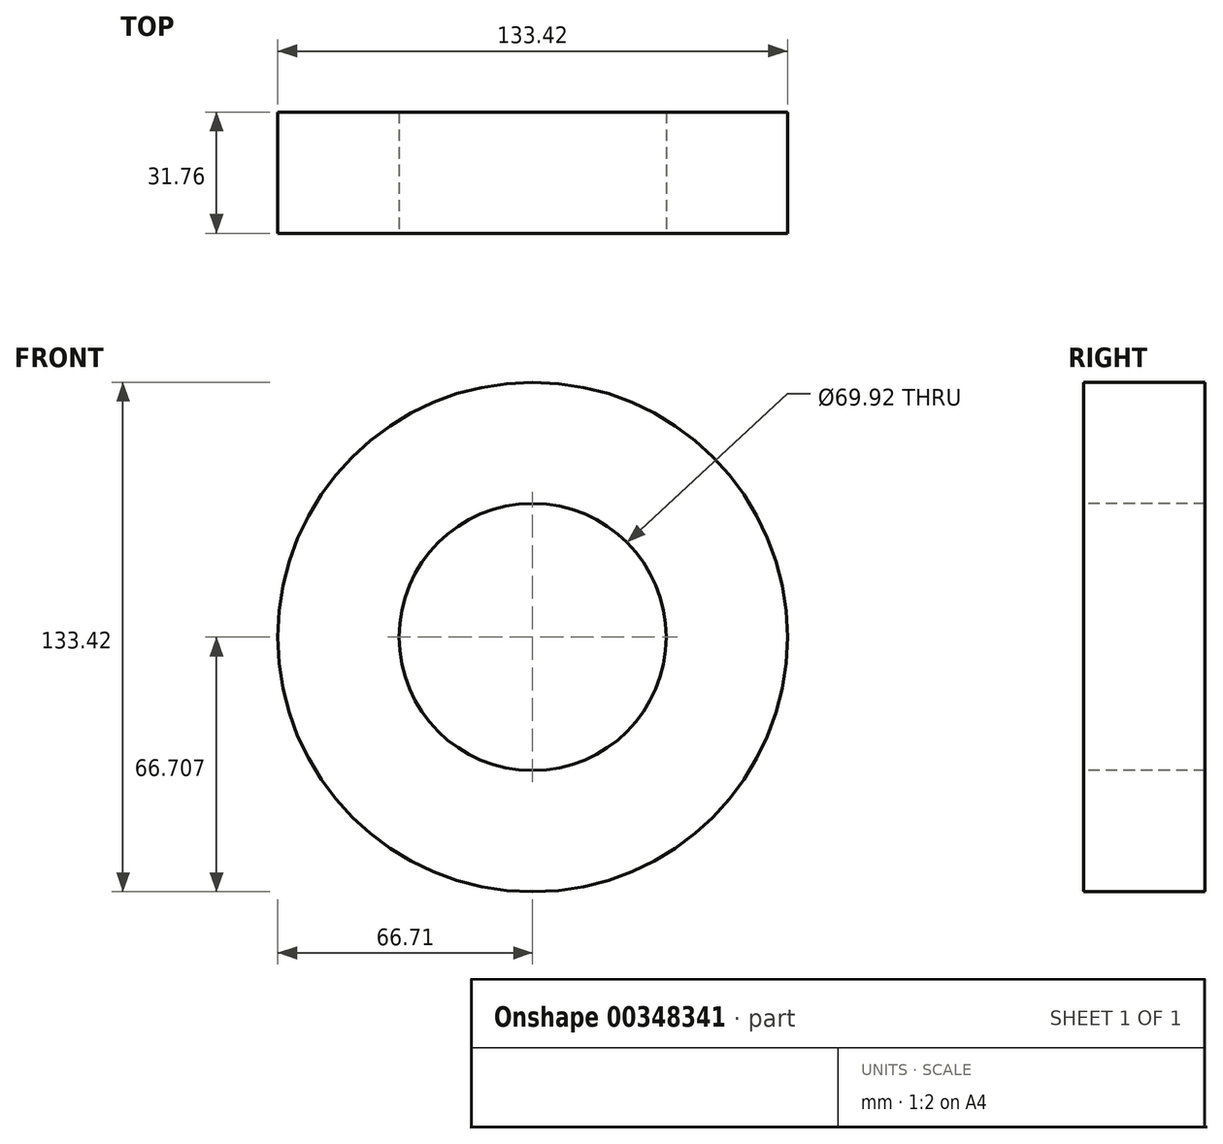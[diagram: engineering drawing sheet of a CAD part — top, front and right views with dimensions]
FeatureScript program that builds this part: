
annotation { "Feature Type Name" : "Feature", "Feature Type Description" : "" }
export const myFeature = defineFeature(function(context is Context, id is Id, definition is map)
    precondition{}
    {
        {
            var Q0;
            Q0=qCreatedBy(makeId("Right.planeOp"),FACE);
            var sketch = newSketch(context, id + "F0", { "sketchPlane" : qUnion([Q0])});
            skLineSegment(sketch, "E0.bottom", {"start": v(15.88, 15.87) * mm, "end": v(-15.88, 15.87) * mm});
            skLineSegment(sketch, "E0.top", {"start": v(15.88, -15.88) * mm, "end": v(-15.88, -15.88) * mm});
            skLineSegment(sketch, "E0.left", {"start": v(15.88, 15.88) * mm, "end": v(15.88, -15.88) * mm});
            skLineSegment(sketch, "E0.right", {"start": v(-15.88, 15.87) * mm, "end": v(-15.88, -15.88) * mm});
            skPoint(sketch, "E0.middle", {"position": v(0, 0) * mm});
            skSolve(sketch);
        }
        {
            var Q0;
            Q0=qCreatedBy(makeId("Right.planeOp"),FACE);
            var sketch = newSketch(context, id + "F1", { "sketchPlane" : qUnion([Q0])});
            skLineSegment(sketch, "E1", {"start": v(-58.65, -50.83) * mm, "end": v(59.26, -50.83) * mm});
            skSolve(sketch);
        }
        {
            var Q0;
            Q0=makeQuery(id+"F0.imprint","IMPRINT",FACE,{"disambiguationData":[TD([[makeQuery(id+"F0.imprint","IMPRINT",EDGE,{"derivedFrom":sQuery(id+"F0.wireOp",EDGE,"E0.bottom")}),1.0]])]});
            var Q1;
            Q1=sQuery(id+"F1.wireOp",EDGE,"E1");
            revolve(context, id + "F2", {"entities" : qUnion([Q0]), "axis" : qUnion([Q1]), "revolveType" : RevolveType.FULL});
        }
    });
